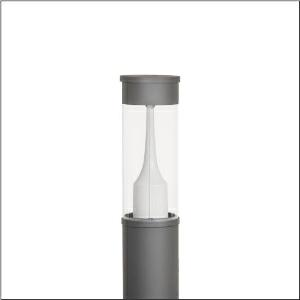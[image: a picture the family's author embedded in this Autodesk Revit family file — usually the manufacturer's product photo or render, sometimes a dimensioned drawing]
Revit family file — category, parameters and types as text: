
# Revit family: city-light_120_iq___p1_0a_5xa5285lf14h_baf3
name_source: partatom
category: Lighting Fixtures
units: mm (PartAtom-declared; Revit-internal decimal feet)

## family parameters
Cut with Voids When Loaded = No
Host = Face
Light Source = No
Part Type = Normal
Room Calculation Point = No
Round Connector Dimension = Use Diameter
Shared = No

## types (1)
- --- (1 x LED, 1510 lm, 10 W, 4000K)
    Apparent Load = 10 VA
    CIE Flux Codes = 32 61 90 93 100
    Color Rendering = 70
    Color Temperature = 4000K
    Default Elevation = 1800 mm
    Description = City-Light 120 iQ, bollard luminaire, Module 540 iQ-SR, primary light control with 3 zone facetted reflector, of plastic, silver coated, highly specular, structured, primary optical cover: cover, of PMMA, transparent, partly coated, light distribution: P1.0a, primary light characteristic: strongly asymmetric, LED, High Power LED, rated luminous flux: 1.510lm, luminous efficacy: 151lm/W, light colour: 740, colour temperature: 4000K, control gear: ECG iQ, control: pre-setting: logarithmic dimming characteristic, Street-Remote, Auto-Match, Temp-Guard, Lumen-Switch, Night-Set, Smart-Wire, Light-Fading, Desk-Remote (wireless, voltage-free reading and setting of iQ features in the workshop via application-optimized NFC function/RFID function), optimised constant luminous flux control (CLO 2.0), with terminal, 6-pole, max. 2.5mm², mains connection: 230..240V, AC, 50/60Hz, start of lifetime: 10W, end of service life: 10W, reduction: 5W, luminaire housing, cylindrical, of extruded aluminium section, coated, Siteco® metallic grey (DB 702S), length: 1.200mm, diameter: 200mm, Module 540 iQ-SR, traffic white (RAL 9016), equipment: standard, protection rating (complete): IP54, insulation class (complete): insulation class II (safety insulation), certification: CE, ENEC, VDE, packaging unit: 1 piece

Light Distribution: P1.0a
    Height = 500 mm
    Lamp = 1 x LED
    Lamp Light Flux = 1510 lm
    Lamp Power = 10 W
    Lamp count = 1
    Length = 200 mm  [stored 0.656168 ft]
    Luminous efficacy = 151 lm/W
    Manufacturer = Siteco
    ModVariant = No
    Model = 5XA5285LF14H
    Mounting Place = Floor
    Mounting Type = Freestanding
    Number of Poles = 1
    OnlyDefault = Yes
    Power Factor = 1
    Product Name = City-Light 120 iQ | P1.0a
    Product group = bollard luminaire
    ProductGroupID = 1304
    Protection Class = Protection class II
    Protection Degree = IP 54
    RLX_Detail_Level = 1
    RLX_Emergency_Light_Flux = 0 lm
    RLX_Emergency_Type = 0
    RLX_Emergency_Type_DB = No
    RlxData = <blob elided: 52745 chars, md5=8dc23e74>
    Socket = socket
    Standby Power = 0 W
    System Light Flux = 1510 lm
    System Power = 10 W
    Type Comments = factory setting: luminous flux: 100 % | dim-lin: 254 | 401 mA
    Type Image = l_1006922.jpg
    URL = http://relux.com
    VarID = @adj_129921
    Voltage = 0 V
    Weight = 0.00 kg
    Width = 0 mm  [stored 0 ft]

note: [stored X ft] marks values corroborated as IEEE doubles in the binary element streams (Revit-internal decimal feet)

## geometry (parser evidence)
native form markers: Blend x4, Sweep x9
no freeform markers — native parametric forms only
